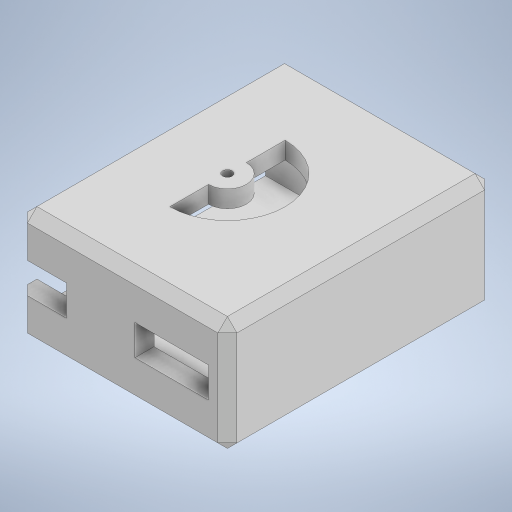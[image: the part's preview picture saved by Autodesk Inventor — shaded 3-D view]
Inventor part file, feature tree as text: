
AUTODESK INVENTOR PART (.ipt)
format: ipt  version: 2023 (Build 270158000, 158)  size: 266,240 bytes
history: native  units: in
note: dims shown in document units (in); Inventor stores cm internally (conversion verified against a paired STEP export)
features: extrude x6, sketch x2, chamfer x1
ambient origin geometry x8: Origin, YZ Plane, XZ Plane, XY Plane, X Axis, Y Axis, Z Axis, Center Point
bodies: Solid1 (feature_tree)
feature tree (9):
  sketch  "Sketch1"  dims[d0=3.0in d1=3.0in]
  extrude  "Extrusion1"  Depth=3.0in
  extrude  "Extrusion2"  Depth=0.25in
  extrude  "Extrusion3"  Depth=0.25in
  extrude  "Extrusion4"  Depth=0.9in
  extrude  "Extrusion5"  Depth=0.9in
  chamfer  "Chamfer1"  Distance=1.5in
  extrude  "Extrusion6"  Depth=1.05in TaperAngle=0.0deg
  sketch  "Sketch2"  dims[d2=0.25in d3=0.25in d4=0.25in d6=0.5in d7=0.24in d8=1.5in d9=0.0in d10=1.05in d11=0.0in d12=0.125in d13=1.05in d14=0.0in d15=1.05in d16=0.0in d17=3.0in d18=0.0in d19=0.125in d20=0.125in d21=45.0deg d22=0.2in d23=0.4in d24=5.0in d25=0.0in d26=0.9634in d27=0.9in]
